# Revit family: 1209 03
name_source: partatom
category: Elektroinstallationen
revit_build: Autodesk Revit 2017 (Build: 20160225_1515(x64)
units: mm (PartAtom-declared; Revit-internal decimal feet)

## family parameters
Basisbauteil = Fläche
Beim Laden mit Abzugskörper schneiden = Nein
Bemaßung runder Anschluss = Durchmesser verwenden
Beschriftungsausrichtung beibehalten = Ja
Gemeinsam genutzt = Nein
Raumberechnungspunkt = Nein
Teiletyp = Normal

## types (1)
- 1209 03
    Abhörsicher = Ja
    Ausführung der Schnittstelle = Sonstige
    BIMSITE_PRODUCT_ID = f71cf4ecf9244ccdea814a23a289702145b9fd6b
    Bedienung Türöffner = Ja
    Beschreibung = Wohnungsstation Video AP 7 Reinweiß glänzend Merkmale:<BR>- Komplett vormontierte Einheit mit einem 17,78 cm (7) großen TFT-Farbdisplay und komfortabler Freisprechfunktion.<BR>- Vollflächige Glasfront mit Touchfunktionalität und taktiler Rückmeldung.<BR>- Direkte Wandmontage oder Wandmontage mit Unterputz-Gerätedose bzw. Hohlwanddose.<BR>- Montage mit Standfuß für Platzierung auf Möbelstücken."
    Bildsystem = PAL
    Datenblatt = http://katalog.gira.de
    Farbe = weiß
    Freisprechen = Ja
    Funktions-Lampen = Nein
    GTIN = 4,01034E+12
    HAN = 120903
    HeinzeBIM = https://www.heinze.de
    Hersteller = Gira
    Hörgerätekompatibel = Nein
    Installationstechnik = 2-Draht
    Internkommunikation = Ja
    Ist System = Nein
    Ist Zubehör = Nein
    Lautstärkeregelung = Ja
    Mit Memory-Funktion = Ja
    Mit Touchscreen = Ja
    Mit Türöffnerautomatik = Ja
    Mit Video = Ja
    Montageart = Tischgerät
    Produktseite = https://katalog.gira.de
    Rufabschaltung = Ja
    Rufunterscheidung = Ja
    Schaltfunktionen = Ja
    Typname = Wohnungsstation Video AP 7 Türko Reinweiß
    URL = https://www.gira.de
    Verbindung mit Smartphone möglich = Nein
    Vorgabe-Ansicht = 1219 mm
    Zusatzgerät anreihbar = Ja

## geometry (parser evidence)
native form markers: Sweep x2
no freeform markers — native parametric forms only
